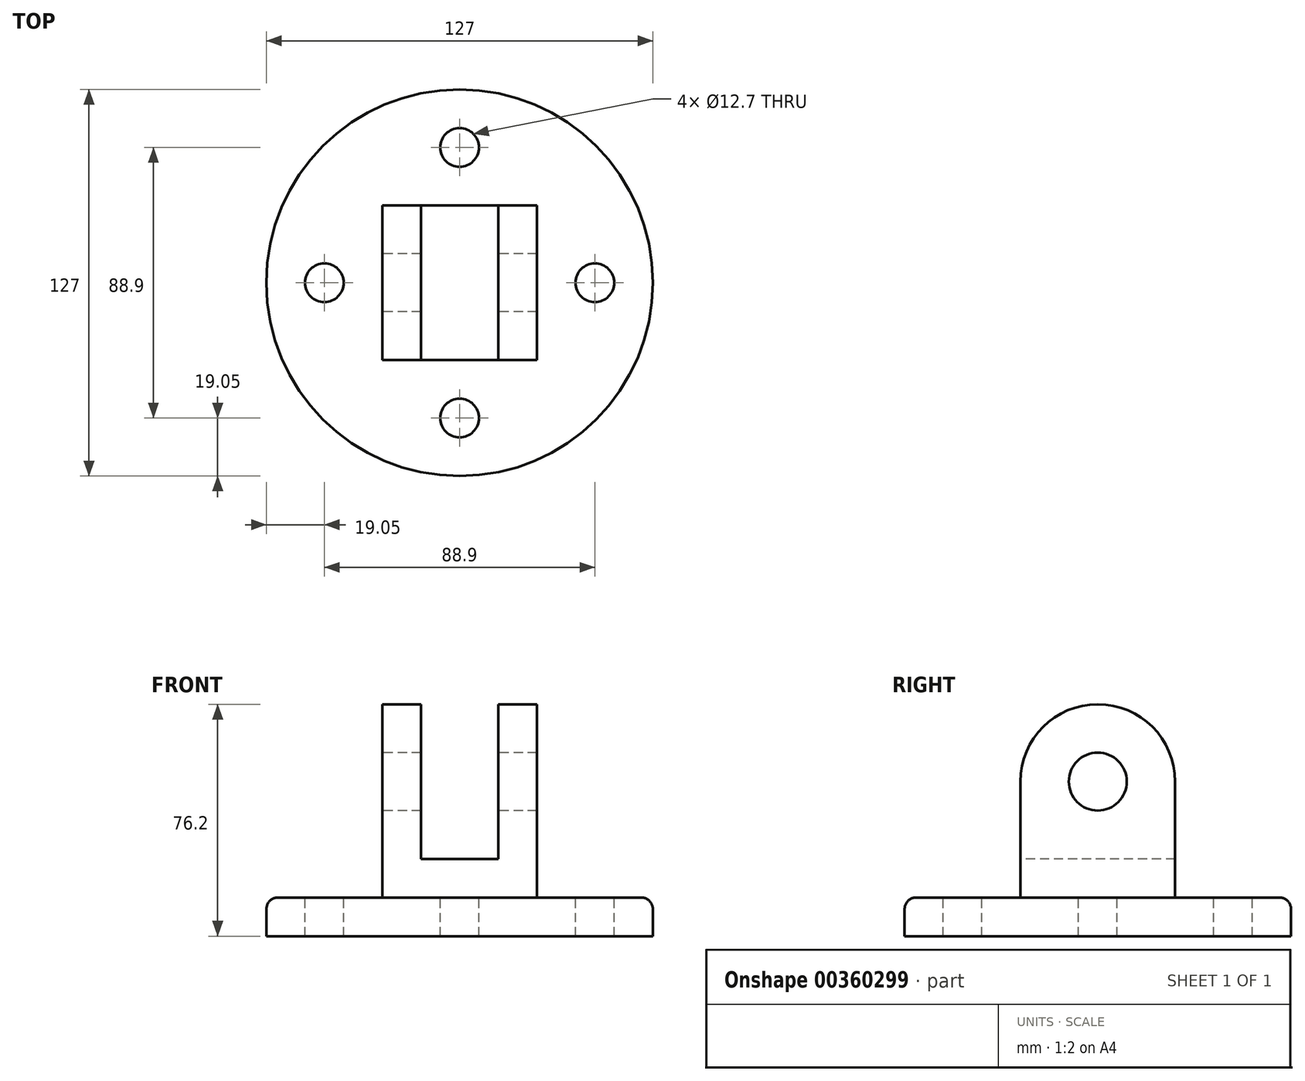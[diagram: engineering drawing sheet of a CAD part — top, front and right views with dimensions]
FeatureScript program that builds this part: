
annotation { "Feature Type Name" : "Feature", "Feature Type Description" : "" }
export const myFeature = defineFeature(function(context is Context, id is Id, definition is map)
    precondition{}
    {
        {
            var Q0;
            Q0=qCreatedBy(makeId("Right.planeOp"),FACE);
            var sketch = newSketch(context, id + "F0", { "sketchPlane" : qUnion([Q0])});
            skLineSegment(sketch, "E0", {"start": v(0, 0) * mm, "end": v(0, 38.1) * mm});
            skLineSegment(sketch, "E1", {"start": v(0, 0) * mm, "end": v(50.8, 0) * mm});
            skLineSegment(sketch, "E2", {"start": v(50.8, 0) * mm, "end": v(50.8, 38.1) * mm});
            skArc(sketch, "E3", {"start": v(50.8, 38.1) * mm, "mid": v(25.4, 63.5) * mm, "end": v(0, 38.1) * mm});
            skCircle(sketch, "E4", {"center": v(25.4, 38.1) * mm, "radius": 9.53 * mm});
            skSolve(sketch);
        }
        {
            var Q0;
            Q0 = qSketchRegion(id + "F0", true);
            extrude(context, id + "F1", {"entities" : qUnion([Q0]), "depth" : 50.8 * mm});
        }
        {
            var Q0;
            Q0=makeQuery(id+"F1.opExtrude","SWEPT_FACE",FACE,{"disambiguationData":[OSD([sQuery(id+"F0.wireOp",EDGE,"E0")])]});
            var sketch = newSketch(context, id + "F2", { "sketchPlane" : qUnion([Q0])});
            skLineSegment(sketch, "E5.bottom", {"start": v(12.7, 12.7) * mm, "end": v(38.1, 12.7) * mm});
            skLineSegment(sketch, "E5.top", {"start": v(12.7, 88.9) * mm, "end": v(38.1, 88.9) * mm});
            skLineSegment(sketch, "E5.left", {"start": v(12.7, 12.7) * mm, "end": v(12.7, 88.9) * mm});
            skLineSegment(sketch, "E5.right", {"start": v(38.1, 12.7) * mm, "end": v(38.1, 88.9) * mm});
            skSolve(sketch);
        }
        {
            var Q0;
            Q0 = qSketchRegion(id + "F2", true);
            extrude(context, id + "F3", {"entities" : qUnion([Q0]), "operationType" : NewBodyOperationType.REMOVE, "endBound" : BoundingType.THROUGH_ALL, "oppositeDirection" : true, "depth" : 25.4 * mm});
        }
        {
            var Q0;
            Q0=makeQuery(id+"F1.opExtrude","SWEPT_FACE",FACE,{"disambiguationData":[OSD([sQuery(id+"F0.wireOp",EDGE,"E1")])]});
            var sketch = newSketch(context, id + "F4", { "sketchPlane" : qUnion([Q0])});
            skCircle(sketch, "E6", {"center": v(25.4, -25.4) * mm, "radius": 63.5 * mm});
            skPoint(sketch, "E6.centerSnap0", {"position": v(25.4, 0) * mm});
            skPoint(sketch, "E6.centerSnap1", {"position": v(0, -25.4) * mm});
            skCircle(sketch, "E7", {"center": v(25.4, 19.05) * mm, "radius": 6.35 * mm});
            skCircle(sketch, "E8", {"center": v(69.85, -25.4) * mm, "radius": 6.35 * mm});
            skPoint(sketch, "E8.centerSnap0", {"position": v(50.8, -25.4) * mm});
            skCircle(sketch, "E9", {"center": v(-19.05, -25.4) * mm, "radius": 6.35 * mm});
            skCircle(sketch, "E10", {"center": v(25.4, -69.85) * mm, "radius": 6.35 * mm});
            skPoint(sketch, "E10.centerSnap0", {"position": v(25.4, -50.8) * mm});
            skSolve(sketch);
        }
        {
            var Q0;
            Q0=makeQuery(id+"F4.imprint","IMPRINT",FACE,{"disambiguationData":[TD([[makeQuery(id+"F4.imprint","IMPRINT",EDGE,{"derivedFrom":sQuery(id+"F4.wireOp",EDGE,"E6")}),1.0]])]});
            var Q1;
            {var subQ0=sQuery(id+"F0.wireOp",EDGE,"E1");Q1=makeQuery(id+"F4.imprint","IMPRINT",FACE,{"disambiguationData":[TD([[makeQuery(id+"F4.imprint","IMPRINT",EDGE,{"derivedFrom":makeQuery(id+"F1.opExtrude","CAP_EDGE",EDGE,{"disambiguationData":[OSD([subQ0])],"isStart":true})}),1.0]])]});}
            extrude(context, id + "F5", {"entities" : qUnion([Q0, Q1]), "operationType" : NewBodyOperationType.ADD, "depth" : 12.7 * mm});
        }
        {
            var Q0;
            Q0=makeQuery(id+"F1.opExtrude","CAP_EDGE",EDGE,{"disambiguationData":[OSD([sQuery(id+"F0.wireOp",EDGE,"E1")])],"isStart":false});
            var Q1;
            Q1=makeQuery(id+"F1.opExtrude","SWEPT_EDGE",EDGE,{"disambiguationData":[OSD([sQuery(id+"F0.wireOp",EDGE,"E0"),sQuery(id+"F0.wireOp",EDGE,"E1")])]});
            var Q2;
            Q2=makeQuery(id+"F1.opExtrude","SWEPT_EDGE",EDGE,{"disambiguationData":[OSD([sQuery(id+"F0.wireOp",EDGE,"E1"),sQuery(id+"F0.wireOp",EDGE,"E2")])]});
            var Q3;
            Q3=makeQuery(id+"F1.opExtrude","CAP_EDGE",EDGE,{"disambiguationData":[OSD([sQuery(id+"F0.wireOp",EDGE,"E1")])],"isStart":true});
            var Q4;
            Q4=makeQuery(id+"F5.opExtrude","CAP_EDGE",EDGE,{"disambiguationData":[OSD([sQuery(id+"F4.wireOp",EDGE,"E6")])],"isStart":true});
            fillet(context, id + "F6", {"entities" : qUnion([Q0, Q1, Q2, Q3, Q4]), "radius" : 3.8 * mm, "tangentPropagation" : true, "allowEdgeOverflow" : false});
        }
    });
